# Revit family: QF_BPRO_TS 1 18-33 Kids_574766
name_source: partatom
category: Sonderausstattung
revit_build: Autodesk Revit 2018 (Build: 20190510_1515(x64)
units: mm (PartAtom-declared; Revit-internal decimal feet)

## family parameters
Arbeitsebenenbasiert = Nein
Beim Laden mit Abzugskörper schneiden = Nein
Bemaßung runder Anschluss = Durchmesser verwenden
Gemeinsam genutzt = Nein
Immer vertikal = Ja
Raumberechnungspunkt = Ja
Teiletyp = Normal

## types (1)
- TS 1 18-33 Kids
    Artikel Nummer = 574766
    Becken Breite = 340 mm  [stored 1.11549 ft]
    Becken Länge = 340 mm  [stored 1.11549 ft]
    Becken Tiefe = 470 mm  [stored 1.54199 ft]
    Beschreibung = Tellerspender Kids, unbeheizt;
mit niedriger Höhe für Kinderverpflegung;
eine quadratische Tellerröhre, komplett entnehmbar;
ca. 60 Teller
    Beschreibung durch Hersteller analog Leistungsverzeichniskurztext = Abmessungen

Länge:				554 mm
Breite:				520 mm
Höhe: (inkl. Tellerführungen)                      880 mm
Arbeitshöhe:	900 mm


Ausführung

Der Spenderkorpus ist komplett in CNS 18/10, Werkstoff-Nr. 1.4301 ausgeführt. Die Oberfläche ist mikroliert. Der Tellerspender ist mit einer quadratischen Tellerröhre ausgestattet. Die Tellerröhre verfügt über eine besonders flache Stapelplattform, die verkantsicher geführt wird.
Mithilfe von vier rilsanbeschichteten Tellerführungsstäben lässt sich diese über ein Lochraster am Boden flexibel und ohne Werkzeug auf unterschiedliche Tellergrößen und Tellerformen einstellen. In der Tellerröhre können beispielsweise runde Teller mit einem Durchmesser von 18 – 33 cm, sowie eckige Teller bis maximal 28 x 28 cm gestapelt werden.
Die Tellerführungsstäbe ragen über die Abdeckung des Spenders hinaus. Dadurch können mehr Teller sicher transportiert und abgestapelt werden. 
Zur einfachen Reinigung des Spenders sowie zum einfachen und ergonomischen Einstellen der Federspannung ist die Tellerröhre komplett aus dem Korpus entnehmbar. 
Durch Ein- bzw. Aushängen der Zugfedern kann die Federspannung entsprechend dem Stapelgut reguliert werden, um eine gleichbleibende Ausgabehöhe zu gewährleisten. 
Durch spezielle Aussparungen an den Federhaltern lässt sich diese Einstellung schnell und ohne großen Aufwand durchführen. 
Bedienseitig ist ein CNS-Sicherheits-Schiebegriff mit seitlichen, robusten Stoßschutzelementen aus Kunststoff angebracht. Mit einem Rohrdurchmesser von 28 mm ermöglicht dieser ein ergonomisches und benutzerfreundliches Schieben des Spenders. 
Der Spender ist fahrbar mittels rostfreien Kunststoffrollen (4 Lenkrollen, davon 2 mit Feststeller, Rollendurchmesser 125 mm).
Robuste Stoßecken aus Kunststoff an allen vier Ecken des Spenders schützen Gerät und Mobiliar vor Beschädigungen. 


Zubehör/ Optionen

•	Transparente Abdeckhaube aus Polycarbonat
•	Isolierte Abdeckhaube aus EPP, silbergrau 
•	Halteclip für Abdeckhauben
(zum Anclipsen an den Schiebegriff. Bietet Platz für 2 Abdeckhauben aus Polycarbonat bzw. 1 Abdeckhaube aus EPP)
•	Nachfüllsignal
(Zeigt dem Personal rechtzeitig an, wenn die Teller in der entsprechenden Röhre zu Ende gehen)
•	Umlaufender Stoßschutz
•	4 zusätzliche Tellerführungen pro Röhre
(Mithilfe der zusätzlichen Tellerführungen können in der Tellerröhre 4 Stapel kleine Geschirrteile wie bspw. Salat-, Dessert-, oder Suppenschalen abgestapelt werden. Die zusätzlichen Tellerführungen unterstützen zudem bei der Abstapelung ausgefallener Tellerformen)
•	GN-Einhängerahmen stirnseitig
(Bietet Platz für 3 Stk. Gastronormbehälter GN 1/6)
•	Reinigungsschublade
•	Korpus aus CNS pulverbeschichtet in verschiedenen Farben. 
•	Weitere Rollenausführungen siehe Gesamtpreisliste


Technische Daten

Werkstoff:		CNS 18/10, Werkstoff-Nr. 
                                             1.4301
Gewicht:		ca. 34 kg
Max. Zuladung:		65 kg
Kapazität:		ca. 60 Teller (abhängig  von der Stapelhöhe)
Geschirrmaße:		Rund: Ø 18-33 cm
		Eckig: max. 28x28 cm
Anzahl Röhren:		1
Stapelhöhe mit
Abdeckhaube:			650 mm
Stapelhöhe ohne
Abdeckhaube:			635 mm



Besonderheit

•	Große, quadratische Tellerröhre für hohe Flexibilität bei der Bestückung mit unterschiedlichen Tellergrößen und Tellerformen
•	Besonders flache, verkantsicher geführte Stapelplattform
•	Hohe Führungsstangen für sicheren Halt der Teller auch ohne Abdeckhaube
•	Entnehmbare Tellerröhre für optimale Hygiene und einfaches Handling
•	Einfache Federeinstellung durch das Easy-Setting System



Fabrikat

Hersteller:	B.PRO
Typ:	TS-1 18-33 Kids
Best.-Nr.:	574766
    Beschreibung durch Hersteller analog Leistungsverzeichnislangtext = Abmessungen

Länge:				554 mm
Breite:				520 mm
Höhe: (inkl. Tellerführungen)                      880 mm
Arbeitshöhe:	900 mm


Ausführung

Der Spenderkorpus ist komplett in CNS 18/10, Werkstoff-Nr. 1.4301 ausgeführt. Die Oberfläche ist mikroliert. Der Tellerspender ist mit einer quadratischen Tellerröhre ausgestattet. Die Tellerröhre verfügt über eine besonders flache Stapelplattform, die verkantsicher geführt wird.
Mithilfe von vier rilsanbeschichteten Tellerführungsstäben lässt sich diese über ein Lochraster am Boden flexibel und ohne Werkzeug auf unterschiedliche Tellergrößen und Tellerformen einstellen. In der Tellerröhre können beispielsweise runde Teller mit einem Durchmesser von 18 – 33 cm, sowie eckige Teller bis maximal 28 x 28 cm gestapelt werden.
Die Tellerführungsstäbe ragen über die Abdeckung des Spenders hinaus. Dadurch können mehr Teller sicher transportiert und abgestapelt werden. 
Zur einfachen Reinigung des Spenders sowie zum einfachen und ergonomischen Einstellen der Federspannung ist die Tellerröhre komplett aus dem Korpus entnehmbar. 
Durch Ein- bzw. Aushängen der Zugfedern kann die Federspannung entsprechend dem Stapelgut reguliert werden, um eine gleichbleibende Ausgabehöhe zu gewährleisten. 
Durch spezielle Aussparungen an den Federhaltern lässt sich diese Einstellung schnell und ohne großen Aufwand durchführen. 
Bedienseitig ist ein CNS-Sicherheits-Schiebegriff mit seitlichen, robusten Stoßschutzelementen aus Kunststoff angebracht. Mit einem Rohrdurchmesser von 28 mm ermöglicht dieser ein ergonomisches und benutzerfreundliches Schieben des Spenders. 
Der Spender ist fahrbar mittels rostfreien Kunststoffrollen (4 Lenkrollen, davon 2 mit Feststeller, Rollendurchmesser 125 mm).
Robuste Stoßecken aus Kunststoff an allen vier Ecken des Spenders schützen Gerät und Mobiliar vor Beschädigungen. 


Zubehör/ Optionen

•	Transparente Abdeckhaube aus Polycarbonat
•	Isolierte Abdeckhaube aus EPP, silbergrau 
•	Halteclip für Abdeckhauben
(zum Anclipsen an den Schiebegriff. Bietet Platz für 2 Abdeckhauben aus Polycarbonat bzw. 1 Abdeckhaube aus EPP)
•	Nachfüllsignal
(Zeigt dem Personal rechtzeitig an, wenn die Teller in der entsprechenden Röhre zu Ende gehen)
•	Umlaufender Stoßschutz
•	4 zusätzliche Tellerführungen pro Röhre
(Mithilfe der zusätzlichen Tellerführungen können in der Tellerröhre 4 Stapel kleine Geschirrteile wie bspw. Salat-, Dessert-, oder Suppenschalen abgestapelt werden. Die zusätzlichen Tellerführungen unterstützen zudem bei der Abstapelung ausgefallener Tellerformen)
•	GN-Einhängerahmen stirnseitig
(Bietet Platz für 3 Stk. Gastronormbehälter GN 1/6)
•	Reinigungsschublade
•	Korpus aus CNS pulverbeschichtet in verschiedenen Farben. 
•	Weitere Rollenausführungen siehe Gesamtpreisliste


Technische Daten

Werkstoff:		CNS 18/10, Werkstoff-Nr. 
                                             1.4301
Gewicht:		ca. 34 kg
Max. Zuladung:		65 kg
Kapazität:		ca. 60 Teller (abhängig  von der Stapelhöhe)
Geschirrmaße:		Rund: Ø 18-33 cm
		Eckig: max. 28x28 cm
Anzahl Röhren:		1
Stapelhöhe mit
Abdeckhaube:			650 mm
Stapelhöhe ohne
Abdeckhaube:			635 mm



Besonderheit

•	Große, quadratische Tellerröhre für hohe Flexibilität bei der Bestückung mit unterschiedlichen Tellergrößen und Tellerformen
•	Besonders flache, verkantsicher geführte Stapelplattform
•	Hohe Führungsstangen für sicheren Halt der Teller auch ohne Abdeckhaube
•	Entnehmbare Tellerröhre für optimale Hygiene und einfaches Handling
•	Einfache Federeinstellung durch das Easy-Setting System



Fabrikat

Hersteller:	B.PRO
Typ:	TS-1 18-33 Kids
Best.-Nr.:	574766
    Gerätegewicht Netto = 34.00 kg
    Großküchengerätezuordnung = Ja
    Hersteller = B.PRO GmbH
    Höhe = 880 mm  [stored 2.88714 ft]
    Höhe Korpus = 750 mm  [stored 2.46063 ft]
    Internetadresse Gerätehersteller = https://www.bpro-solutions.com
    Internetadresse für Ersatzteilliste = https://www.bpro-solutions.com
    Kosten = 1182.5 $
    Länge Gerätebreite = 554 mm  [stored 1.81759 ft]
    Länge Korpus = 450 mm  [stored 1.47638 ft]
    Material = QF_Metal-Stainless-Steel_general
    Material_Stoßschutz = QF_Rubber-Black-Matt
    Modell = TS 1 18-33 Kids
    Sockelhöhe = 161 mm  [stored 0.528215 ft]
    Tiefe = 520 mm  [stored 1.70604 ft]
    Tiefe Korpus = 450 mm  [stored 1.47638 ft]
    Typenkommentare = Tellerspender Kids, unbeheizt 1-fach
    URL = https://www.bpro-solutions.com
    Warnhinweise = Ausführliche Gefahrenhinweise entnehmen Sie der Betriebsanleitung.
    Zubehör = Nein

note: [stored X ft] marks values corroborated as IEEE doubles in the binary element streams (Revit-internal decimal feet)
